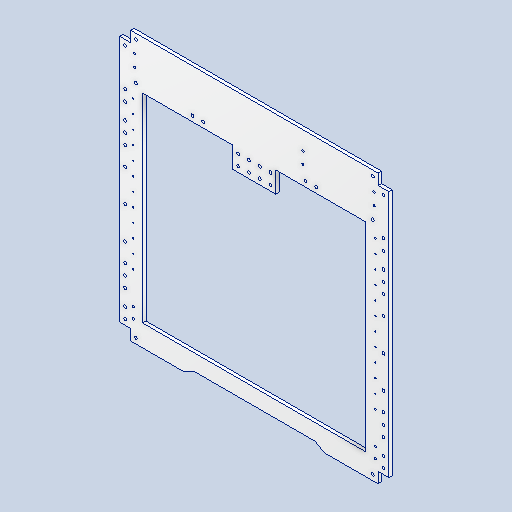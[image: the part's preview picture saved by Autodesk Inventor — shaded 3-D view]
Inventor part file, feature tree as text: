
AUTODESK INVENTOR PART (.ipt)
format: ipt  version: 2024 (Build 280153000, 153)  size: 739,840 bytes
history: native  units: mm
features: sketch x8, projected_geometry x6, hole x5, extrude x4, mirror x1
ambient origin geometry x8: Origin, YZ Plane, XZ Plane, XY Plane, X Axis, Y Axis, Z Axis, Center Point
bodies: Solid1 (feature_tree)
feature tree (24):
  sketch  "Sketch1"  dims[d0=506.5mm d1=506.5mm]
  extrude  "Extrusion1"  Depth=506.5mm
  hole  "Hole1"  [1 undecoded]
  extrude  "Extrusion2"  Depth=40.0mm
  sketch  "Sketch4"  dims[d6=3.25mm d7=3.25mm]
  extrude  "Extrusion3"  Depth=3.25mm
  extrude  "Extrusion4"  Depth=20.0mm
  hole  "Hole2"  [1 undecoded]
  mirror  "Mirror1"
  hole  "Hole3"  [1 undecoded]
  hole  "Hole4"  [1 undecoded]
  hole  "Hole5"  [1 undecoded]
  sketch  "Sketch3"  dims[d4=40.0mm d5=40.0mm]
  sketch  "Sketch2"  dims[d2=20.0mm d3=20.0mm]
  projected_geometry  "Projected Loop1"
  projected_geometry  "Projected Loop2"
  sketch  "Sketch5"  dims[d8=20.0mm d9=20.0mm]
  projected_geometry  "Projected Loop3"
  sketch  "Sketch6"  dims[d10=3.25mm d11=3.25mm]
  projected_geometry  "Projected Loop4"
  sketch  "Sketch7"  dims[d12=3.25mm d13=3.25mm]
  projected_geometry  "Projected Loop5"
  sketch  "Sketch8"  dims[d14=3.25mm d15=3.25mm d16=3.25mm d17=70.0mm d18=80.0mm d19=40.0mm d20=60.0mm d21=20.0mm d22=20.0mm d23=20.0mm d24=40.0mm d25=20.0mm d27=85.0mm d28=20.0mm d30=20.0mm d34=6.35mm d35=0.0mm d36=5.3mm d37=6.0mm d38=4.0mm d39=2.0mm d40=90.0deg d41=8.0mm d42=20.594885mm d43=20.0mm d44=20.0mm d47=0.0mm d48=0.0mm d49=50.0mm d50=42.0mm d56=300.0mm d57=250.0mm d59=50.0mm d60=400.0mm d61=12.0mm d62=12.0mm d63=300.0mm d64=15.0mm d65=27.0mm d66=45.0mm d67=40.0mm d68=40.0mm d70=80.0mm d71=80.0mm d72=10.0mm d73=150.0deg d74=0.0mm d75=0.0mm d78=4.0mm d81=80.0mm d82=40.0mm d83=40.0mm d84=40.0mm d85=40.0mm d86=40.0mm d87=40.0mm d88=20.0mm d89=40.0mm d90=20.0mm d91=0.0mm d92=0.0mm d93=4.0mm d94=4.0mm d95=120.0mm d97=25.0mm d98=10.0mm d100=10.0mm d102=12.0mm d103=300.0mm d104=25.0mm d105=95.0mm d106=2.459mm d107=6.0mm d108=4.0mm d109=2.0mm d110=90.0deg d111=8.0mm d112=20.594885mm d113=85.0mm d115=50.0mm d120=22.0mm d121=34.0mm d122=27.5mm d123=4.134mm d124=10.0mm d125=4.0mm d126=2.0mm d127=90.0deg d128=8.0mm d129=20.594885mm d131=132.0mm d132=415.0mm d133=20.0mm d134=25.0mm d135=18.0mm d136=1.0mm d137=50.0mm d138=50.0mm d139=50.0mm d140=170.0mm d141=170.0mm d142=30.0mm d143=30.0mm d144=30.0mm d145=30.0mm d146=5.4mm d147=6.0mm d148=4.0mm d149=2.0mm d150=90.0deg d151=8.0mm d152=20.594885mm d153=120.0mm d154=5.4mm d155=6.0mm d156=4.0mm d157=2.0mm d158=90.0deg d159=8.0mm d160=20.594885mm]
  projected_geometry  "Projected Loop6"
note: 5 required parameter values undecoded (feature->parameter linkage not recoverable at this tier; creation-order binding heuristic only, values carry confidence <= 0.55)
